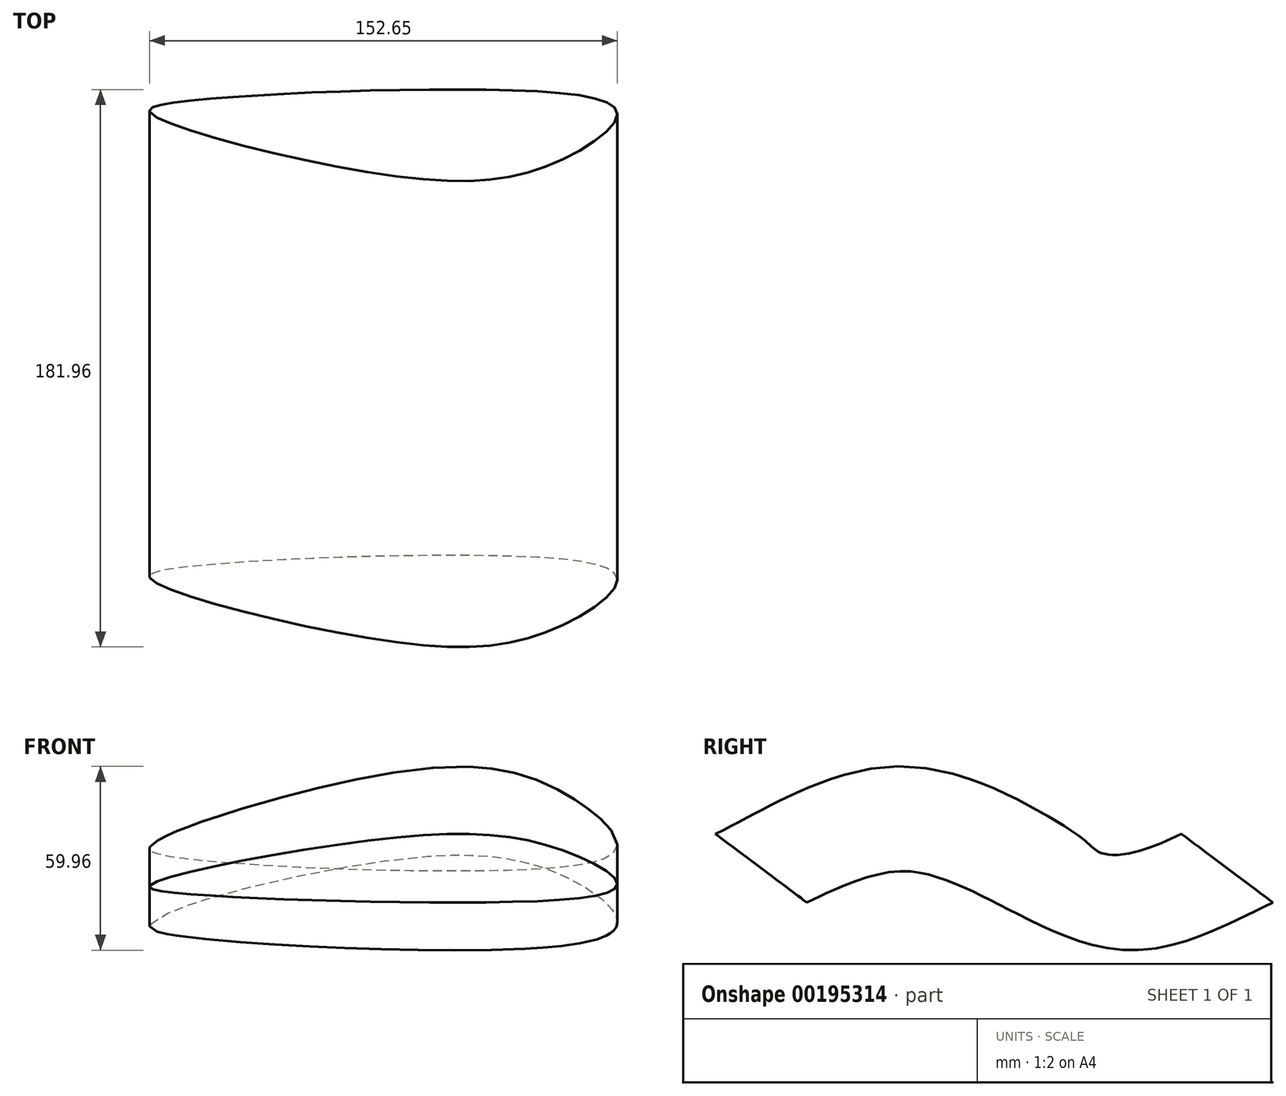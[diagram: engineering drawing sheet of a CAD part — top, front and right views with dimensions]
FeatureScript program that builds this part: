
annotation { "Feature Type Name" : "Feature", "Feature Type Description" : "" }
export const myFeature = defineFeature(function(context is Context, id is Id, definition is map)
    precondition{}
    {
        {
            var Q0;
            Q0=qCreatedBy(makeId("Front.planeOp"),FACE);
            var sketch = newSketch(context, id + "F0", { "sketchPlane" : qUnion([Q0])});
            skLineSegment(sketch, "E0", {"start": v(0, 0) * mm, "end": v(76.2, 0) * mm, "construction": true});
            skLineSegment(sketch, "E1.MirrorCS", {"start": v(0, 0) * mm, "end": v(-76.2, 0) * mm, "construction": true});
            skLineSegment(sketch, "E2", {"start": v(0, 0) * mm, "end": v(0, 50.8) * mm, "construction": true});
            skFitSpline(sketch, "E3", {"points": [v(-76.2, 0) * mm, v(0, 25.4) * mm, v(55.5, 20.81) * mm, v(76.2, 0) * mm, v(34.96, -9.16) * mm, v(-66.04, -4.35) * mm, v(-76.2, 0) * mm]});
            skSolve(sketch);
        }
        {
            var Q0;
            Q0=qCreatedBy(makeId("Right.planeOp"),FACE);
            var sketch = newSketch(context, id + "F1", { "sketchPlane" : qUnion([Q0])});
            skFitSpline(sketch, "E4", {"points": [v(0, 0) * mm, v(-37.18, 12.67) * mm, v(-76.03, 0) * mm], "startDerivative": vector(-74.65, 38.14) * mm, "endDerivative": vector(-77.4, -37.9) * mm});
            skFitSpline(sketch, "E5.MirrorCS", {"points": [v(0, 0) * mm, v(37.18, -12.67) * mm, v(76.03, 0) * mm], "startDerivative": vector(74.65, -38.14) * mm, "endDerivative": vector(77.4, 37.9) * mm});
            skSolve(sketch);
        }
        {
            var Q0;
            Q0=makeQuery(id+"F0.imprint","IMPRINT",FACE,{"disambiguationData":[TD([[makeQuery(id+"F0.imprint","IMPRINT",EDGE,{"derivedFrom":sQuery(id+"F0.wireOp",EDGE,"E3")}),-1.0]])]});
            var Q1;
            Q1=sQuery(id+"F1.wireOp",EDGE,"E4");
            sweep(context, id + "F2", {"profiles" : qUnion([Q0]), "path" : qUnion([Q1])});
        }
        {
            var Q0;
            Q0=makeQuery(id+"F2.opSweep","CAP_FACE",FACE,{"disambiguationData":[OSD([sQuery(id+"F0.wireOp",EDGE,"E3"),sQuery(id+"F1.wireOp",VERTEX,"E4.start")])],"isStart":true});
            var Q1;
            Q1=sQuery(id+"F1.wireOp",EDGE,"E5.MirrorCS");
            sweep(context, id + "F3", {"operationType" : NewBodyOperationType.ADD, "profiles" : qUnion([Q0]), "path" : qUnion([Q1])});
        }
    });
